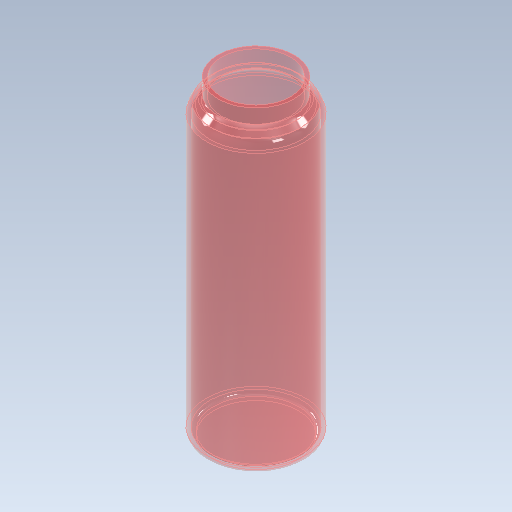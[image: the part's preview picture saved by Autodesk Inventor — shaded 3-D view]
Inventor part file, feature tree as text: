
AUTODESK INVENTOR PART (.ipt)
format: ipt  version: 2021 (Build 250183000, 183)  size: 160,768 bytes
history: native  units: mm
features: extrude x2, fillet x2, sketch x2, chamfer x1, shell x1
ambient origin geometry x8: Origin, YZ Plane, XZ Plane, XY Plane, X Axis, Y Axis, Z Axis, Center Point
bodies: Solid1 (feature_tree)
feature tree (8):
  extrude  "Extrusion1"  Depth=82.0mm TaperAngle=0.0deg
  extrude  "Extrusion2"  Depth=4.0mm TaperAngle=0.0deg
  chamfer  "Chamfer1"  Distance=3.0mm Angle=45.0deg
  fillet  "Fillet1"  Radius=4.0mm
  fillet  "Fillet2"  Radius=2.0mm
  shell  "Shell1"  Thickness=1.0mm
  sketch  "Sketch1"  dims[d0=27.5mm d1=82.0mm d2=0.0mm]
  sketch  "Sketch2"  dims[d3=21.1mm d4=4.0mm d5=0.0mm d6=3.0mm d7=2.0mm d8=45.0deg d9=4.0mm d10=2.0mm d11=1.0mm]
